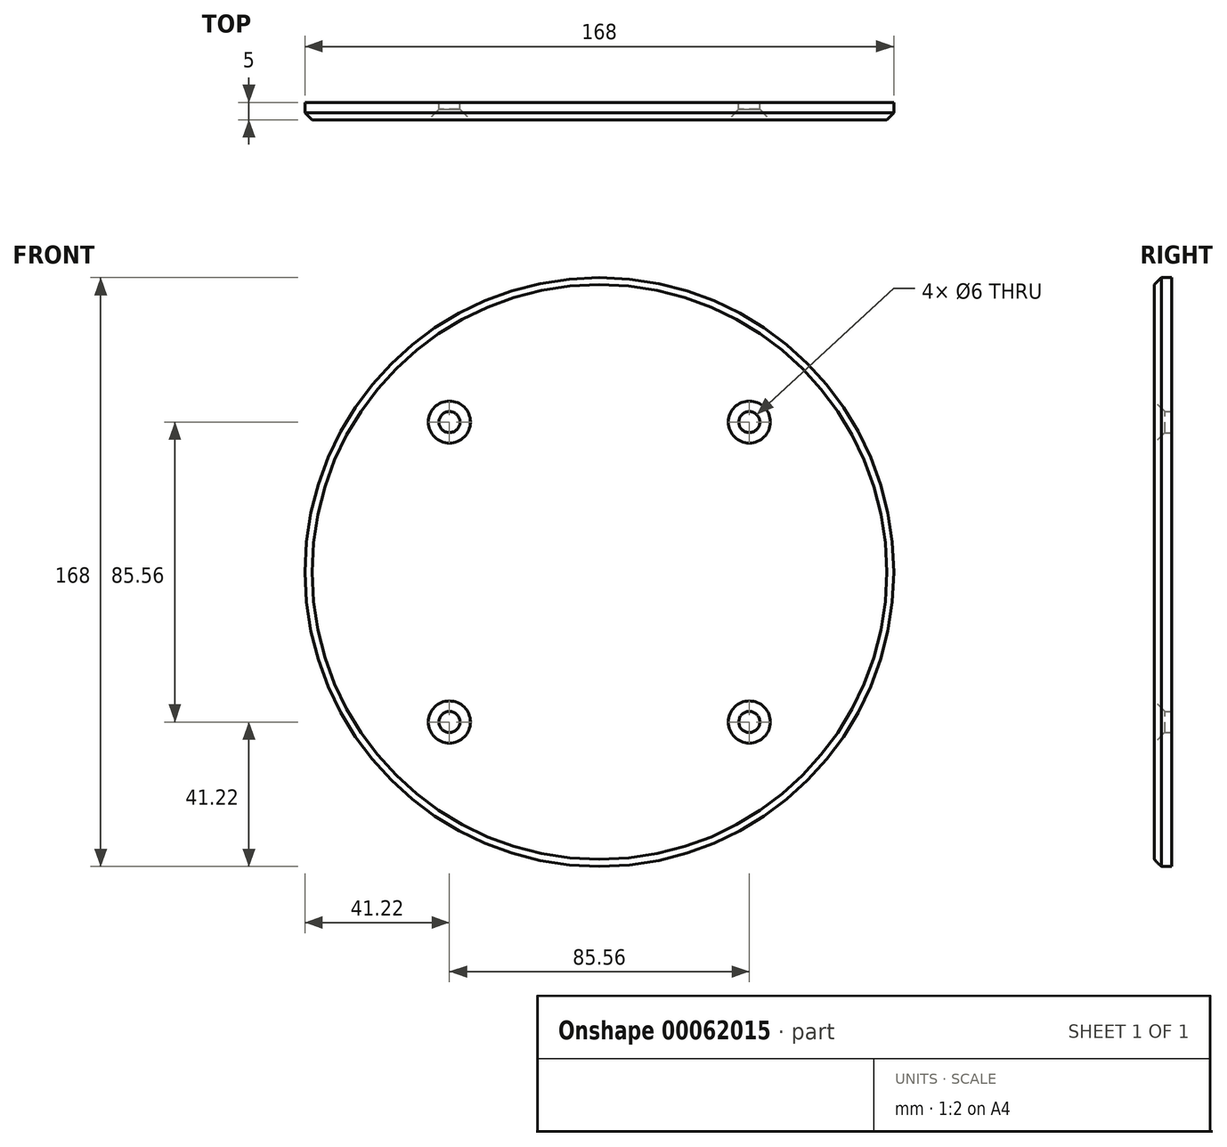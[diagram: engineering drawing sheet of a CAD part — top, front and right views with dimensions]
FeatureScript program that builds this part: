
annotation { "Feature Type Name" : "Feature", "Feature Type Description" : "" }
export const myFeature = defineFeature(function(context is Context, id is Id, definition is map)
    precondition{}
    {
        {
            var Q0;
            Q0=qCreatedBy(makeId("Front.planeOp"),FACE);
            var sketch = newSketch(context, id + "F0", { "sketchPlane" : qUnion([Q0])});
            skCircle(sketch, "E0", {"center": v(0, 0) * mm, "radius": 81 * mm, "construction": true});
            skCircle(sketch, "E1", {"center": v(0, 0) * mm, "radius": 63.5 * mm, "construction": true});
            skCircle(sketch, "E2", {"center": v(0, 0) * mm, "radius": 60.5 * mm, "construction": true});
            skCircle(sketch, "E3", {"center": v(42.78, -42.78) * mm, "radius": 3 * mm});
            skCircle(sketch, "E4", {"center": v(-42.78, -42.78) * mm, "radius": 3 * mm});
            skCircle(sketch, "E5", {"center": v(42.78, 42.78) * mm, "radius": 3 * mm});
            skLineSegment(sketch, "E6", {"start": v(-42.78, 42.78) * mm, "end": v(0, 0) * mm, "construction": true});
            skLineSegment(sketch, "E7", {"start": v(42.78, 42.78) * mm, "end": v(0, 0) * mm, "construction": true});
            skLineSegment(sketch, "E8", {"start": v(0, 0) * mm, "end": v(42.78, -42.78) * mm, "construction": true});
            skCircle(sketch, "E9", {"center": v(-42.78, 42.78) * mm, "radius": 3 * mm});
            skCircle(sketch, "E10", {"center": v(0, 0) * mm, "radius": 84 * mm});
            skCircle(sketch, "E11", {"center": v(0, 60.5) * mm, "radius": 3 * mm, "construction": true});
            skSolve(sketch);
        }
        {
            var Q0;
            Q0=qSketchRegion(id+"F0",true);
            extrude(context, id + "F1", {"entities" : qUnion([Q0]), "depth" : 5 * mm});
        }
        {
            var Q0;
            Q0=makeQuery(id+"F1.opExtrude","CAP_EDGE",EDGE,{"disambiguationData":[OSD([sQuery(id+"F0.wireOp",EDGE,"45f90977-bbc4-4781-ba83-c9ce9f726cbe")])],"isStart":true});
            var Q1;
            Q1=makeQuery(id+"F1.opExtrude","CAP_EDGE",EDGE,{"disambiguationData":[OSD([sQuery(id+"F0.wireOp",EDGE,"E10")])],"isStart":false});
            chamfer(context, id + "F2", {"entities" : qUnion([Q0, Q1]), "width" : 2 * mm, "tangentPropagation" : true});
        }
        {
            var Q0;
            Q0=makeQuery(id+"F1.opExtrude","CAP_EDGE",EDGE,{"disambiguationData":[OSD([sQuery(id+"F0.wireOp",EDGE,"E9")])],"isStart":false});
            var Q1;
            Q1=makeQuery(id+"F1.opExtrude","CAP_EDGE",EDGE,{"disambiguationData":[OSD([sQuery(id+"F0.wireOp",EDGE,"E5")])],"isStart":false});
            var Q2;
            Q2=makeQuery(id+"F1.opExtrude","CAP_EDGE",EDGE,{"disambiguationData":[OSD([sQuery(id+"F0.wireOp",EDGE,"E4")])],"isStart":false});
            var Q3;
            Q3=makeQuery(id+"F1.opExtrude","CAP_EDGE",EDGE,{"disambiguationData":[OSD([sQuery(id+"F0.wireOp",EDGE,"E3")])],"isStart":false});
            chamfer(context, id + "F3", {"entities" : qUnion([Q0, Q1, Q2, Q3]), "width" : 3 * mm});
        }
    });
